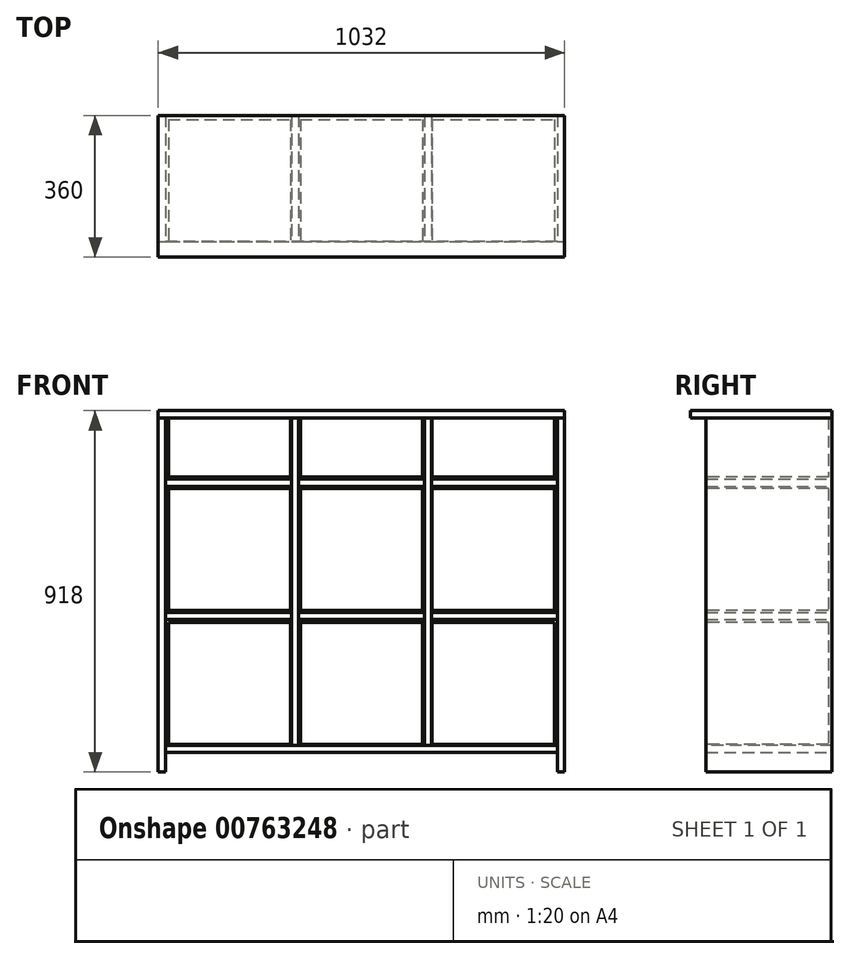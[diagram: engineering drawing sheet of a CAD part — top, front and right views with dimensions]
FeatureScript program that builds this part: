
annotation { "Feature Type Name" : "Feature", "Feature Type Description" : "" }
export const myFeature = defineFeature(function(context is Context, id is Id, definition is map)
    precondition{}
    {
        {
            var Q0;
            Q0=qCreatedBy(makeId("Top.planeOp"),FACE);
            var sketch = newSketch(context, id + "F0", { "sketchPlane" : qUnion([Q0])});
            skLineSegment(sketch, "E0.bottom", {"start": v(-516, 120) * mm, "end": v(-498, 120) * mm});
            skLineSegment(sketch, "E0.top", {"start": v(-516, -200) * mm, "end": v(-498, -200) * mm});
            skLineSegment(sketch, "E0.left", {"start": v(-516, 120) * mm, "end": v(-516, -200) * mm});
            skLineSegment(sketch, "E0.right", {"start": v(-498, 120) * mm, "end": v(-498, -200) * mm});
            skLineSegment(sketch, "E1.bottom", {"start": v(498, 120) * mm, "end": v(516, 120) * mm});
            skLineSegment(sketch, "E1.top", {"start": v(498, -200) * mm, "end": v(516, -200) * mm});
            skLineSegment(sketch, "E1.left", {"start": v(498, 120) * mm, "end": v(498, -200) * mm});
            skLineSegment(sketch, "E1.right", {"start": v(516, 120) * mm, "end": v(516, -200) * mm});
            skSolve(sketch);
        }
        {
            var Q0;
            Q0 = qSketchRegion(id + "F0", true);
            extrude(context, id + "F1", {"entities" : qUnion([Q0]), "depth" : 900 * mm, "offsetDistance" : 25 * mm});
        }
        {
            var Q0;
            Q0=qCreatedBy(makeId("Top.planeOp"),FACE);
            cPlane(context, id + "F2", {"entities" : qUnion([Q0]), "cplaneType" : CPlaneType.OFFSET, "offset" : 68 * mm, "width" : 150 * mm, "height" : 150 * mm});
        }
        {
            var Q0;
            Q0=qCreatedBy(id+"F2.planeOp",FACE);
            var sketch = newSketch(context, id + "F3", { "sketchPlane" : qUnion([Q0])});
            skLineSegment(sketch, "E2.bottom", {"start": v(-178, 120) * mm, "end": v(-160, 120) * mm});
            skLineSegment(sketch, "E2.top", {"start": v(-178, -200) * mm, "end": v(-160, -200) * mm});
            skLineSegment(sketch, "E2.left", {"start": v(-178, 120) * mm, "end": v(-178, -200) * mm});
            skLineSegment(sketch, "E2.right", {"start": v(-160, 120) * mm, "end": v(-160, -200) * mm});
            skLineSegment(sketch, "E3.bottom", {"start": v(160, 120) * mm, "end": v(178, 120) * mm});
            skLineSegment(sketch, "E3.top", {"start": v(160, -200) * mm, "end": v(178, -200) * mm});
            skLineSegment(sketch, "E3.left", {"start": v(160, 120) * mm, "end": v(160, -200) * mm});
            skLineSegment(sketch, "E3.right", {"start": v(178, 120) * mm, "end": v(178, -200) * mm});
            skSolve(sketch);
        }
        {
            var Q0;
            Q0 = qSketchRegion(id + "F3", true);
            extrude(context, id + "F4", {"entities" : qUnion([Q0]), "depth" : 832 * mm, "offsetDistance" : 25 * mm});
        }
        {
            var Q0;
            Q0=qCreatedBy(makeId("Right.planeOp"),FACE);
            var sketch = newSketch(context, id + "F5", { "sketchPlane" : qUnion([Q0])});
            skLineSegment(sketch, "E4.bottom", {"start": v(-200, 68) * mm, "end": v(120, 68) * mm});
            skLineSegment(sketch, "E4.top", {"start": v(-200, 50) * mm, "end": v(120, 50) * mm});
            skLineSegment(sketch, "E4.left", {"start": v(-200, 68) * mm, "end": v(-200, 50) * mm});
            skLineSegment(sketch, "E4.right", {"start": v(120, 68) * mm, "end": v(120, 50) * mm});
            skLineSegment(sketch, "E5.bottom", {"start": v(-240, 918) * mm, "end": v(120, 918) * mm});
            skLineSegment(sketch, "E5.top", {"start": v(-240, 900) * mm, "end": v(120, 900) * mm});
            skLineSegment(sketch, "E5.left", {"start": v(-240, 918) * mm, "end": v(-240, 900) * mm});
            skLineSegment(sketch, "E5.right", {"start": v(120, 918) * mm, "end": v(120, 900) * mm});
            skSolve(sketch);
        }
        {
            var Q0;
            Q0=makeQuery(id+"F5.imprint","IMPRINT",FACE,{"disambiguationData":[TD([[makeQuery(id+"F5.imprint","IMPRINT",EDGE,{"derivedFrom":sQuery(id+"F5.wireOp",EDGE,"E4.bottom")}),-1.0]])]});
            extrude(context, id + "F6", {"entities" : qUnion([Q0]), "endBound" : BoundingType.SYMMETRIC, "depth" : 996 * mm, "offsetDistance" : 25 * mm});
        }
        {
            var Q0;
            Q0=qCreatedBy(makeId("Right.planeOp"),FACE);
            cPlane(context, id + "F7", {"entities" : qUnion([Q0]), "cplaneType" : CPlaneType.OFFSET, "offset" : 178 * mm, "oppositeDirection" : true, "width" : 150 * mm, "height" : 150 * mm});
        }
        {
            var Q0;
            Q0=qCreatedBy(makeId("Right.planeOp"),FACE);
            cPlane(context, id + "F8", {"entities" : qUnion([Q0]), "cplaneType" : CPlaneType.OFFSET, "offset" : 160 * mm, "width" : 150 * mm, "height" : 150 * mm});
        }
        {
            var Q0;
            Q0=qCreatedBy(makeId("Right.planeOp"),FACE);
            cPlane(context, id + "F9", {"entities" : qUnion([Q0]), "cplaneType" : CPlaneType.OFFSET, "offset" : 498 * mm, "width" : 150 * mm, "height" : 150 * mm});
        }
        {
            var Q0;
            Q0=qCreatedBy(id+"F7.planeOp",FACE);
            var sketch = newSketch(context, id + "F10", { "sketchPlane" : qUnion([Q0])});
            skLineSegment(sketch, "E6.bottom", {"start": v(-200, 406) * mm, "end": v(120, 406) * mm});
            skLineSegment(sketch, "E6.top", {"start": v(-200, 388) * mm, "end": v(120, 388) * mm});
            skLineSegment(sketch, "E6.left", {"start": v(-200, 406) * mm, "end": v(-200, 388) * mm});
            skLineSegment(sketch, "E6.right", {"start": v(120, 406) * mm, "end": v(120, 388) * mm});
            skLineSegment(sketch, "E7.bottom", {"start": v(-200, 726) * mm, "end": v(120, 726) * mm});
            skLineSegment(sketch, "E7.top", {"start": v(-200, 744) * mm, "end": v(120, 744) * mm});
            skLineSegment(sketch, "E7.left", {"start": v(-200, 726) * mm, "end": v(-200, 744) * mm});
            skLineSegment(sketch, "E7.right", {"start": v(120, 726) * mm, "end": v(120, 744) * mm});
            skSolve(sketch);
        }
        {
            var Q0;
            Q0 = qSketchRegion(id + "F10", true);
            extrude(context, id + "F11", {"entities" : qUnion([Q0]), "oppositeDirection" : true, "depth" : 320 * mm, "offsetDistance" : 25 * mm});
        }
        {
            var Q0;
            Q0=qCreatedBy(id+"F8.planeOp",FACE);
            var sketch = newSketch(context, id + "F12", { "sketchPlane" : qUnion([Q0])});
            skLineSegment(sketch, "E8.bottom", {"start": v(-200, 406) * mm, "end": v(120, 406) * mm});
            skLineSegment(sketch, "E8.top", {"start": v(-200, 388) * mm, "end": v(120, 388) * mm});
            skLineSegment(sketch, "E8.left", {"start": v(-200, 406) * mm, "end": v(-200, 388) * mm});
            skLineSegment(sketch, "E8.right", {"start": v(120, 406) * mm, "end": v(120, 388) * mm});
            skLineSegment(sketch, "E9.bottom", {"start": v(-200, 744) * mm, "end": v(120, 744) * mm});
            skLineSegment(sketch, "E9.top", {"start": v(-200, 726) * mm, "end": v(120, 726) * mm});
            skLineSegment(sketch, "E9.left", {"start": v(-200, 744) * mm, "end": v(-200, 726) * mm});
            skLineSegment(sketch, "E9.right", {"start": v(120, 744) * mm, "end": v(120, 726) * mm});
            skSolve(sketch);
        }
        {
            var Q0;
            Q0 = qSketchRegion(id + "F12", true);
            extrude(context, id + "F13", {"entities" : qUnion([Q0]), "oppositeDirection" : true, "depth" : 320 * mm, "offsetDistance" : 25 * mm});
        }
        {
            var Q0;
            Q0=qCreatedBy(id+"F9.planeOp",FACE);
            var sketch = newSketch(context, id + "F14", { "sketchPlane" : qUnion([Q0])});
            skLineSegment(sketch, "E10.bottom", {"start": v(-200, 406) * mm, "end": v(120, 406) * mm});
            skLineSegment(sketch, "E10.top", {"start": v(-200, 388) * mm, "end": v(120, 388) * mm});
            skLineSegment(sketch, "E10.left", {"start": v(-200, 406) * mm, "end": v(-200, 388) * mm});
            skLineSegment(sketch, "E10.right", {"start": v(120, 406) * mm, "end": v(120, 388) * mm});
            skLineSegment(sketch, "E11.bottom", {"start": v(-200, 744) * mm, "end": v(120, 744) * mm});
            skLineSegment(sketch, "E11.top", {"start": v(-200, 726) * mm, "end": v(120, 726) * mm});
            skLineSegment(sketch, "E11.left", {"start": v(-200, 744) * mm, "end": v(-200, 726) * mm});
            skLineSegment(sketch, "E11.right", {"start": v(120, 744) * mm, "end": v(120, 726) * mm});
            skSolve(sketch);
        }
        {
            var Q0;
            Q0 = qSketchRegion(id + "F14", true);
            extrude(context, id + "F15", {"entities" : qUnion([Q0]), "oppositeDirection" : true, "depth" : 320 * mm, "offsetDistance" : 25 * mm});
        }
        {
            var Q0;
            Q0=makeQuery(id+"F5.imprint","IMPRINT",FACE,{"disambiguationData":[TD([[makeQuery(id+"F5.imprint","IMPRINT",EDGE,{"derivedFrom":sQuery(id+"F5.wireOp",EDGE,"E5.bottom")}),-1.0]])]});
            extrude(context, id + "F16", {"entities" : qUnion([Q0]), "endBound" : BoundingType.SYMMETRIC, "depth" : 1032 * mm, "offsetDistance" : 25 * mm});
        }
        {
            var Q0;
            Q0=qCreatedBy(makeId("Top.planeOp"),FACE);
            cPlane(context, id + "F17", {"entities" : qUnion([Q0]), "cplaneType" : CPlaneType.OFFSET, "offset" : 70 * mm, "width" : 150 * mm, "height" : 150 * mm});
        }
        {
            var Q0;
            Q0=qCreatedBy(id+"F17.planeOp",FACE);
            var sketch = newSketch(context, id + "F18", { "sketchPlane" : qUnion([Q0])});
            skLineSegment(sketch, "E12.bottom", {"start": v(-490, 110) * mm, "end": v(-180, 110) * mm});
            skLineSegment(sketch, "E12.top", {"start": v(-490, -200) * mm, "end": v(-180, -200) * mm});
            skLineSegment(sketch, "E12.left", {"start": v(-490, 110) * mm, "end": v(-490, -200) * mm});
            skLineSegment(sketch, "E12.right", {"start": v(-180, 110) * mm, "end": v(-180, -200) * mm});
            skLineSegment(sketch, "E13.bottom", {"start": v(-155, 110) * mm, "end": v(155, 110) * mm});
            skLineSegment(sketch, "E13.top", {"start": v(-155, -200) * mm, "end": v(155, -200) * mm});
            skLineSegment(sketch, "E13.left", {"start": v(-155, 110) * mm, "end": v(-155, -200) * mm});
            skLineSegment(sketch, "E13.right", {"start": v(155, 110) * mm, "end": v(155, -200) * mm});
            skLineSegment(sketch, "E14.bottom", {"start": v(180, 110) * mm, "end": v(490, 110) * mm});
            skLineSegment(sketch, "E14.top", {"start": v(180, -200) * mm, "end": v(490, -200) * mm});
            skLineSegment(sketch, "E14.left", {"start": v(180, 110) * mm, "end": v(180, -200) * mm});
            skLineSegment(sketch, "E14.right", {"start": v(490, 110) * mm, "end": v(490, -200) * mm});
            skSolve(sketch);
        }
        {
            var Q0;
            Q0 = qSketchRegion(id + "F18", true);
            extrude(context, id + "F19", {"entities" : qUnion([Q0]), "depth" : 310 * mm, "offsetDistance" : 25 * mm});
        }
        {
            var Q0;
            Q0=qCreatedBy(id+"F17.planeOp",FACE);
            cPlane(context, id + "F20", {"entities" : qUnion([Q0]), "cplaneType" : CPlaneType.OFFSET, "offset" : 340 * mm, "width" : 150 * mm, "height" : 150 * mm});
        }
        {
            var Q0;
            Q0=qCreatedBy(id+"F20.planeOp",FACE);
            var sketch = newSketch(context, id + "F21", { "sketchPlane" : qUnion([Q0])});
            skLineSegment(sketch, "E15.bottom", {"start": v(-490, 110) * mm, "end": v(-180, 110) * mm});
            skLineSegment(sketch, "E15.top", {"start": v(-490, -200) * mm, "end": v(-180, -200) * mm});
            skLineSegment(sketch, "E15.left", {"start": v(-490, 110) * mm, "end": v(-490, -200) * mm});
            skLineSegment(sketch, "E15.right", {"start": v(-180, 110) * mm, "end": v(-180, -200) * mm});
            skLineSegment(sketch, "E16.bottom", {"start": v(-155, 110) * mm, "end": v(155, 110) * mm});
            skLineSegment(sketch, "E16.top", {"start": v(-155, -200) * mm, "end": v(155, -200) * mm});
            skLineSegment(sketch, "E16.left", {"start": v(-155, 110) * mm, "end": v(-155, -200) * mm});
            skLineSegment(sketch, "E16.right", {"start": v(155, 110) * mm, "end": v(155, -200) * mm});
            skLineSegment(sketch, "E17.bottom", {"start": v(180, 110) * mm, "end": v(490, 110) * mm});
            skLineSegment(sketch, "E17.top", {"start": v(180, -200) * mm, "end": v(490, -200) * mm});
            skLineSegment(sketch, "E17.left", {"start": v(180, 110) * mm, "end": v(180, -200) * mm});
            skLineSegment(sketch, "E17.right", {"start": v(490, 110) * mm, "end": v(490, -200) * mm});
            skSolve(sketch);
        }
        {
            var Q0;
            Q0 = qSketchRegion(id + "F21", true);
            extrude(context, id + "F22", {"entities" : qUnion([Q0]), "depth" : 310 * mm, "offsetDistance" : 25 * mm});
        }
        {
            var Q0;
            Q0=qCreatedBy(id+"F20.planeOp",FACE);
            cPlane(context, id + "F23", {"entities" : qUnion([Q0]), "cplaneType" : CPlaneType.OFFSET, "offset" : 340 * mm, "width" : 150 * mm, "height" : 150 * mm});
        }
        {
            var Q0;
            Q0=qCreatedBy(id+"F23.planeOp",FACE);
            var sketch = newSketch(context, id + "F24", { "sketchPlane" : qUnion([Q0])});
            skLineSegment(sketch, "E18.bottom", {"start": v(-490, 110) * mm, "end": v(-180, 110) * mm});
            skLineSegment(sketch, "E18.top", {"start": v(-490, -200) * mm, "end": v(-180, -200) * mm});
            skLineSegment(sketch, "E18.left", {"start": v(-490, 110) * mm, "end": v(-490, -200) * mm});
            skLineSegment(sketch, "E18.right", {"start": v(-180, 110) * mm, "end": v(-180, -200) * mm});
            skLineSegment(sketch, "E19.bottom", {"start": v(-155, 110) * mm, "end": v(155, 110) * mm});
            skLineSegment(sketch, "E19.top", {"start": v(-155, -200) * mm, "end": v(155, -200) * mm});
            skLineSegment(sketch, "E19.left", {"start": v(-155, 110) * mm, "end": v(-155, -200) * mm});
            skLineSegment(sketch, "E19.right", {"start": v(155, 110) * mm, "end": v(155, -200) * mm});
            skLineSegment(sketch, "E20.bottom", {"start": v(180, 110) * mm, "end": v(490, 110) * mm});
            skLineSegment(sketch, "E20.top", {"start": v(180, -200) * mm, "end": v(490, -200) * mm});
            skLineSegment(sketch, "E20.left", {"start": v(180, 110) * mm, "end": v(180, -200) * mm});
            skLineSegment(sketch, "E20.right", {"start": v(490, 110) * mm, "end": v(490, -200) * mm});
            skSolve(sketch);
        }
        {
            var Q0;
            Q0 = qSketchRegion(id + "F24", true);
            extrude(context, id + "F25", {"entities" : qUnion([Q0]), "depth" : 150 * mm, "offsetDistance" : 25 * mm});
        }
    });
